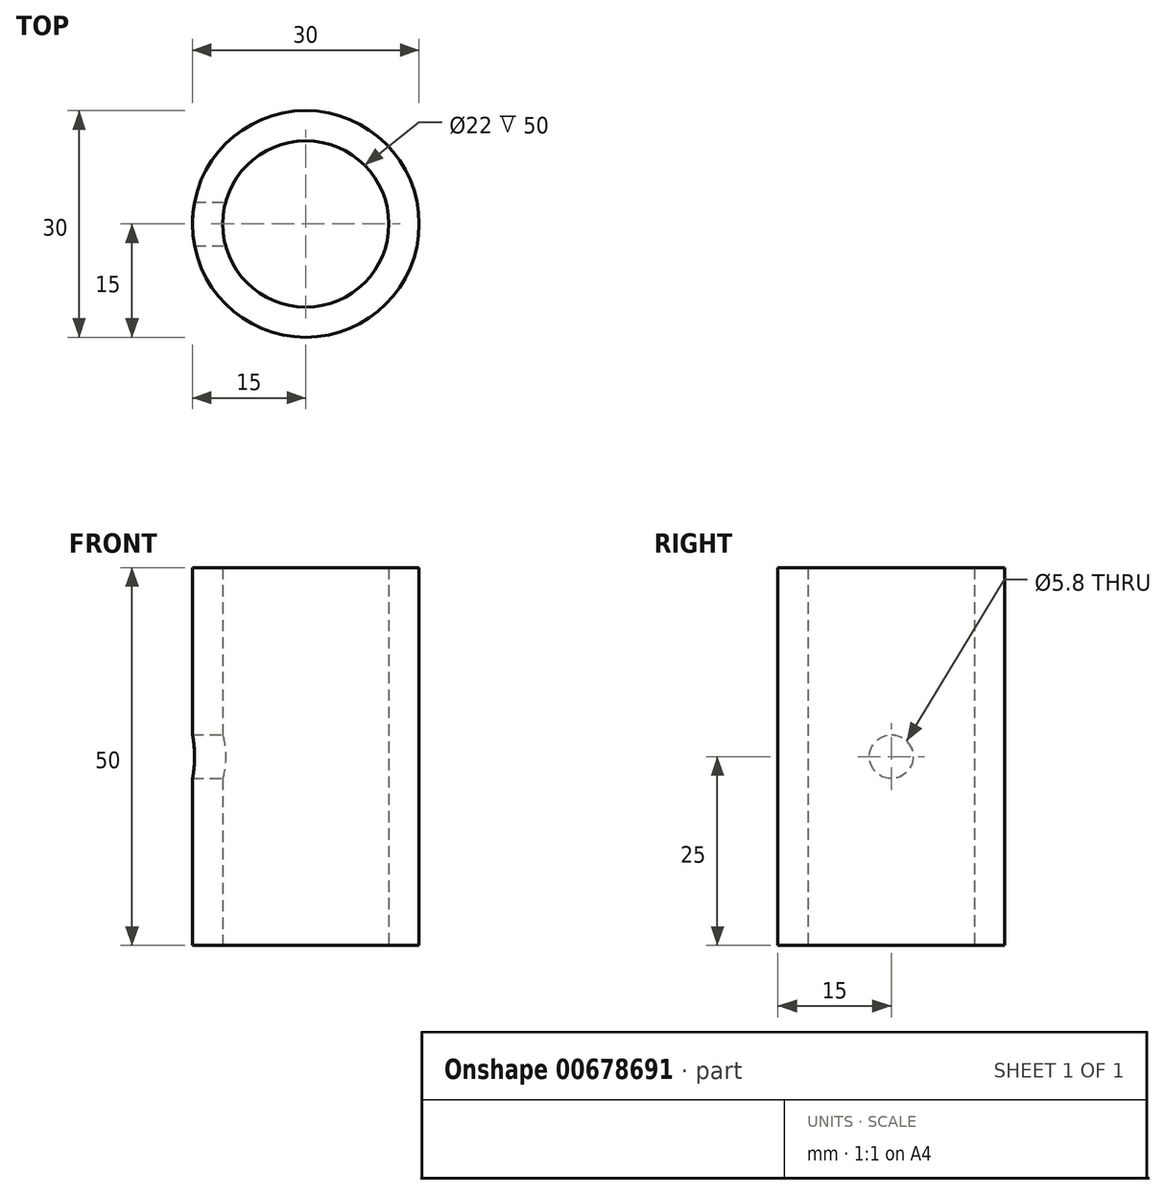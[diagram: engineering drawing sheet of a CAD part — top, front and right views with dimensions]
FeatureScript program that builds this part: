
annotation { "Feature Type Name" : "Feature", "Feature Type Description" : "" }
export const myFeature = defineFeature(function(context is Context, id is Id, definition is map)
    precondition{}
    {
        {
            var Q0;
            Q0=qCreatedBy(makeId("Top.planeOp"),FACE);
            var sketch = newSketch(context, id + "F0", { "sketchPlane" : qUnion([Q0])});
            skCircle(sketch, "E0", {"center": v(0, 0) * mm, "radius": 15 * mm});
            skSolve(sketch);
        }
        {
            var Q0;
            Q0=makeQuery(id+"F0.imprint","IMPRINT",FACE,{"disambiguationData":[TD([[makeQuery(id+"F0.imprint","IMPRINT",EDGE,{"derivedFrom":sQuery(id+"F0.wireOp",EDGE,"E0")}),1.0]])]});
            extrude(context, id + "F1", {"entities" : qUnion([Q0]), "depth" : 50 * mm, "offsetDistance" : 25 * mm});
        }
        {
            var Q0;
            Q0=sQuery(id+"F0.wireOp",VERTEX,"E0.center");
            var Q1;
            Q1=makeQuery(id+"F1.opExtrude","SWEPT_BODY",BODY,{"disambiguationData":[OSD([sQuery(id+"F0.wireOp",EDGE,"E0")])]});
            hole(context, id + "F2", {"style" : HoleStyle.SIMPLE, "endStyle" : HoleEndStyle.THROUGH, "oppositeDirection" : true, "holeDiameter" : 22 * mm, "majorDiameter" : 5 * mm, "isTappedThrough" : true, "tappedDepth" : 12 * mm, "tapClearance" : 3, "locations" : qUnion([Q0]), "scope" : qUnion([Q1])});
        }
        {
            var Q0;
            Q0=qCreatedBy(makeId("Right.planeOp"),FACE);
            var sketch = newSketch(context, id + "F3", { "sketchPlane" : qUnion([Q0])});
            skLineSegment(sketch, "E1", {"start": v(0, 50) * mm, "end": v(0, 0) * mm});
            skCircle(sketch, "E2", {"center": v(0, 25) * mm, "radius": 2.9 * mm});
            skSolve(sketch);
        }
        {
            var Q0;
            Q0=sQuery(id+"F3.wireOp",VERTEX,"E2.center");
            var Q1;
            Q1=makeQuery(id+"F1.opExtrude","SWEPT_BODY",BODY,{"disambiguationData":[OSD([sQuery(id+"F0.wireOp",EDGE,"E0")])]});
            hole(context, id + "F4", {"style" : HoleStyle.SIMPLE, "endStyle" : HoleEndStyle.THROUGH, "holeDiameter" : 5.8 * mm, "majorDiameter" : 5 * mm, "isTappedThrough" : true, "tappedDepth" : 12 * mm, "tapClearance" : 3, "locations" : qUnion([Q0]), "scope" : qUnion([Q1])});
        }
    });
